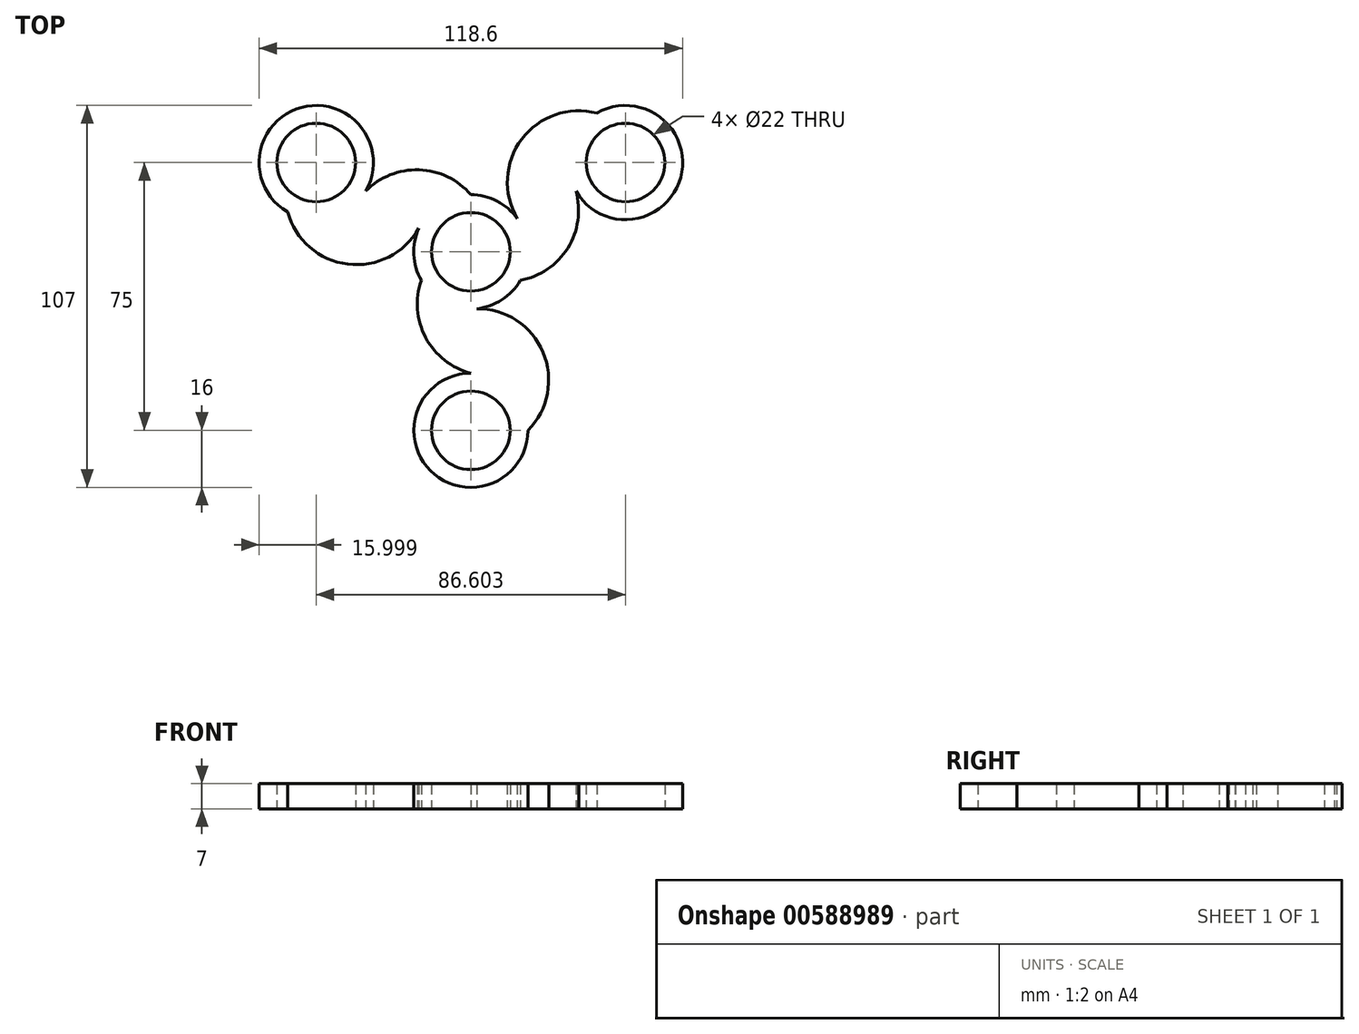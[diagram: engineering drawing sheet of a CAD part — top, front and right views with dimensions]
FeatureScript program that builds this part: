
annotation { "Feature Type Name" : "Feature", "Feature Type Description" : "" }
export const myFeature = defineFeature(function(context is Context, id is Id, definition is map)
    precondition{}
    {
        {
            var Q0;
            Q0=qCreatedBy(makeId("Top.planeOp"),FACE);
            var sketch = newSketch(context, id + "F0", { "sketchPlane" : qUnion([Q0])});
            skCircle(sketch, "E0", {"center": v(0, 0) * mm, "radius": 11 * mm});
            skCircle(sketch, "E1", {"center": v(0, 0) * mm, "radius": 16 * mm});
            skLineSegment(sketch, "E2", {"start": v(0, 0) * mm, "end": v(0, -50) * mm});
            skLineSegment(sketch, "E3", {"start": v(0, 0) * mm, "end": v(43.3, 25) * mm});
            skLineSegment(sketch, "E4", {"start": v(0, 0) * mm, "end": v(-43.3, 25) * mm});
            skCircle(sketch, "E5", {"center": v(-43.3, 25) * mm, "radius": 11 * mm});
            skCircle(sketch, "E6", {"center": v(43.3, 25) * mm, "radius": 11 * mm});
            skCircle(sketch, "E7", {"center": v(0, -50) * mm, "radius": 11 * mm});
            skCircle(sketch, "E8", {"center": v(0, -50) * mm, "radius": 16 * mm});
            skCircle(sketch, "E9", {"center": v(43.3, 25) * mm, "radius": 16 * mm});
            skCircle(sketch, "E10", {"center": v(-43.3, 25) * mm, "radius": 16 * mm});
            skLineSegment(sketch, "E11", {"start": v(0, 0) * mm, "end": v(0, 31.25) * mm});
            skLineSegment(sketch, "E12", {"start": v(0, 0) * mm, "end": v(44.93, 0) * mm});
            skLineSegment(sketch, "E13", {"start": v(0, 0) * mm, "end": v(39.74, -22.94) * mm});
            skLineSegment(sketch, "E14", {"start": v(0, 0) * mm, "end": v(-34.34, -19.83) * mm});
            skArc(sketch, "E15", {"start": v(13.86, -8) * mm, "mid": v(27.14, 1.08) * mm, "end": v(29.44, 17) * mm});
            skArc(sketch, "E16", {"start": v(0, 16) * mm, "mid": v(-14.5, 22.97) * mm, "end": v(-29.44, 17) * mm});
            skArc(sketch, "E17", {"start": v(-13.86, -8) * mm, "mid": v(-12.64, -24.04) * mm, "end": v(0, -34) * mm});
            skLineSegment(sketch, "E18", {"start": v(43.3, 25) * mm, "end": v(31.7, 45.08) * mm});
            skLineSegment(sketch, "E19", {"start": v(-43.3, 25) * mm, "end": v(-53.07, 8.08) * mm});
            skLineSegment(sketch, "E20", {"start": v(0, -50) * mm, "end": v(27.78, -50) * mm});
            skArc(sketch, "E21", {"start": v(35.3, 38.86) * mm, "mid": v(13.79, 30.93) * mm, "end": v(13.86, 8) * mm});
            skArc(sketch, "E22", {"start": v(16, -50) * mm, "mid": v(19.9, -27.4) * mm, "end": v(0, -16) * mm});
            skArc(sketch, "E23", {"start": v(-51.3, 11.14) * mm, "mid": v(-33.68, -3.53) * mm, "end": v(-13.86, 8) * mm});
            skSolve(sketch);
        }
        {
            var Q0;
            {var subQ0=sQuery(id+"F0.wireOp",EDGE,"E21");var subQ1=sQuery(id+"F0.wireOp",EDGE,"E1");var subQ3=makeQuery(id+"F0.imprint","INTERSECT",VERTEX,{"derivedFrom":[subQ1,subQ0]});Q0=makeQuery(id+"F0.imprint","IMPRINT",FACE,{"disambiguationData":[TD([[makeQuery(id+"F0.imprint","IMPRINT",EDGE,{"disambiguationData":[TD([[subQ3,1.0]])],"derivedFrom":subQ1}),1.0]])]});}
            var Q1;
            {var subQ0=sQuery(id+"F0.wireOp",EDGE,"E16");Q1=makeQuery(id+"F0.imprint","IMPRINT",FACE,{"disambiguationData":[TD([[makeQuery(id+"F0.imprint","IMPRINT",EDGE,{"derivedFrom":subQ0}),1.0]])]});}
            var Q2;
            {var subQ0=sQuery(id+"F0.wireOp",EDGE,"E17");Q2=makeQuery(id+"F0.imprint","IMPRINT",FACE,{"disambiguationData":[TD([[makeQuery(id+"F0.imprint","IMPRINT",EDGE,{"derivedFrom":subQ0}),1.0]])]});}
            var Q3;
            {var subQ0=sQuery(id+"F0.wireOp",EDGE,"E22");var subQ1=sQuery(id+"F0.wireOp",EDGE,"E1");var subQ3=makeQuery(id+"F0.imprint","INTERSECT",VERTEX,{"derivedFrom":[subQ1,subQ0]});Q3=makeQuery(id+"F0.imprint","IMPRINT",FACE,{"disambiguationData":[TD([[makeQuery(id+"F0.imprint","IMPRINT",EDGE,{"disambiguationData":[TD([[subQ3,1.0]])],"derivedFrom":subQ1}),1.0]])]});}
            var Q4;
            {var subQ0=sQuery(id+"F0.wireOp",EDGE,"E15");var subQ3=sQuery(id+"F0.wireOp",EDGE,"E12");var subQ5=makeQuery(id+"F0.imprint","INTERSECT",VERTEX,{"derivedFrom":[subQ3,subQ0]});Q4=makeQuery(id+"F0.imprint","IMPRINT",FACE,{"disambiguationData":[TD([[makeQuery(id+"F0.imprint","IMPRINT",EDGE,{"disambiguationData":[TD([[subQ5,1.0]])],"derivedFrom":subQ3}),-1.0]])]});}
            var Q5;
            {var subQ1=sQuery(id+"F0.wireOp",EDGE,"E2");var subQ3=sQuery(id+"F0.wireOp",EDGE,"E7");var subQ4=makeQuery(id+"F0.imprint","INTERSECT",VERTEX,{"derivedFrom":[subQ1,subQ3]});Q5=makeQuery(id+"F0.imprint","IMPRINT",FACE,{"disambiguationData":[TD([[makeQuery(id+"F0.imprint","IMPRINT",EDGE,{"disambiguationData":[TD([[subQ4,-1.0]])],"derivedFrom":subQ3}),-1.0]])]});}
            var Q6;
            {var subQ1=sQuery(id+"F0.wireOp",EDGE,"E3");var subQ3=sQuery(id+"F0.wireOp",EDGE,"E6");var subQ4=makeQuery(id+"F0.imprint","INTERSECT",VERTEX,{"derivedFrom":[subQ1,subQ3]});Q6=makeQuery(id+"F0.imprint","IMPRINT",FACE,{"disambiguationData":[TD([[makeQuery(id+"F0.imprint","IMPRINT",EDGE,{"disambiguationData":[TD([[subQ4,-1.0]])],"derivedFrom":subQ3}),-1.0]])]});}
            var Q7;
            {var subQ1=sQuery(id+"F0.wireOp",EDGE,"E4");var subQ3=sQuery(id+"F0.wireOp",EDGE,"E5");var subQ4=makeQuery(id+"F0.imprint","INTERSECT",VERTEX,{"derivedFrom":[subQ1,subQ3]});Q7=makeQuery(id+"F0.imprint","IMPRINT",FACE,{"disambiguationData":[TD([[makeQuery(id+"F0.imprint","IMPRINT",EDGE,{"disambiguationData":[TD([[subQ4,-1.0]])],"derivedFrom":subQ3}),-1.0]])]});}
            var Q8;
            {var subQ0=sQuery(id+"F0.wireOp",EDGE,"xA9ERZAI-CVpG-Lb7w-0VQH-98zOtqBdUd82");var subQ1=sQuery(id+"F0.wireOp",EDGE,"E0");var subQ2=makeQuery(id+"F0.imprint","INTERSECT",VERTEX,{"derivedFrom":[subQ1,subQ0]});Q8=makeQuery(id+"F0.imprint","IMPRINT",FACE,{"disambiguationData":[TD([[makeQuery(id+"F0.imprint","IMPRINT",EDGE,{"disambiguationData":[TD([[subQ2,-1.0]])],"derivedFrom":subQ1}),-1.0]])]});}
            var Q9;
            {var subQ3=sQuery(id+"F0.wireOp",EDGE,"E12");var subQ5=sQuery(id+"F0.wireOp",EDGE,"E15");var subQ7=makeQuery(id+"F0.imprint","INTERSECT",VERTEX,{"derivedFrom":[subQ3,subQ5]});Q9=makeQuery(id+"F0.imprint","IMPRINT",FACE,{"disambiguationData":[TD([[makeQuery(id+"F0.imprint","IMPRINT",EDGE,{"disambiguationData":[TD([[subQ7,1.0]])],"derivedFrom":subQ3}),1.0]])]});}
            var Q10;
            {var subQ0=sQuery(id+"F0.wireOp",EDGE,"E21");var subQ2=sQuery(id+"F0.wireOp",EDGE,"E1");var subQ4=makeQuery(id+"F0.imprint","INTERSECT",VERTEX,{"derivedFrom":[subQ2,subQ0]});Q10=makeQuery(id+"F0.imprint","IMPRINT",FACE,{"disambiguationData":[TD([[makeQuery(id+"F0.imprint","IMPRINT",EDGE,{"disambiguationData":[TD([[subQ4,1.0]])],"derivedFrom":subQ2}),-1.0]])]});}
            var Q11;
            {var subQ0=sQuery(id+"F0.wireOp",EDGE,"E22");var subQ2=sQuery(id+"F0.wireOp",EDGE,"E1");var subQ4=makeQuery(id+"F0.imprint","INTERSECT",VERTEX,{"derivedFrom":[subQ2,subQ0]});Q11=makeQuery(id+"F0.imprint","IMPRINT",FACE,{"disambiguationData":[TD([[makeQuery(id+"F0.imprint","IMPRINT",EDGE,{"disambiguationData":[TD([[subQ4,1.0]])],"derivedFrom":subQ2}),-1.0]])]});}
            var Q12;
            {var subQ1=sQuery(id+"F0.wireOp",EDGE,"E2");var subQ3=sQuery(id+"F0.wireOp",EDGE,"E7");var subQ4=makeQuery(id+"F0.imprint","INTERSECT",VERTEX,{"derivedFrom":[subQ1,subQ3]});Q12=makeQuery(id+"F0.imprint","IMPRINT",FACE,{"disambiguationData":[TD([[makeQuery(id+"F0.imprint","IMPRINT",EDGE,{"disambiguationData":[TD([[subQ4,1.0]])],"derivedFrom":subQ3}),-1.0]])]});}
            var Q13;
            {var subQ1=sQuery(id+"F0.wireOp",EDGE,"E3");var subQ3=sQuery(id+"F0.wireOp",EDGE,"E6");var subQ4=makeQuery(id+"F0.imprint","INTERSECT",VERTEX,{"derivedFrom":[subQ1,subQ3]});Q13=makeQuery(id+"F0.imprint","IMPRINT",FACE,{"disambiguationData":[TD([[makeQuery(id+"F0.imprint","IMPRINT",EDGE,{"disambiguationData":[TD([[subQ4,1.0]])],"derivedFrom":subQ3}),-1.0]])]});}
            var Q14;
            {var subQ1=sQuery(id+"F0.wireOp",EDGE,"E4");var subQ3=sQuery(id+"F0.wireOp",EDGE,"E5");var subQ4=makeQuery(id+"F0.imprint","INTERSECT",VERTEX,{"derivedFrom":[subQ1,subQ3]});Q14=makeQuery(id+"F0.imprint","IMPRINT",FACE,{"disambiguationData":[TD([[makeQuery(id+"F0.imprint","IMPRINT",EDGE,{"disambiguationData":[TD([[subQ4,1.0]])],"derivedFrom":subQ3}),-1.0]])]});}
            var Q15;
            {var subQ3=sQuery(id+"F0.wireOp",EDGE,"E0");var subQ6=sQuery(id+"F0.wireOp",EDGE,"E3");var subQ8=makeQuery(id+"F0.imprint","INTERSECT",VERTEX,{"derivedFrom":[subQ3,subQ6]});Q15=makeQuery(id+"F0.imprint","IMPRINT",FACE,{"disambiguationData":[TD([[makeQuery(id+"F0.imprint","IMPRINT",EDGE,{"disambiguationData":[TD([[subQ8,-1.0]])],"derivedFrom":subQ3}),-1.0]])]});}
            var Q16;
            {var subQ0=sQuery(id+"F0.wireOp",EDGE,"E11");var subQ1=sQuery(id+"F0.wireOp",EDGE,"E0");var subQ2=makeQuery(id+"F0.imprint","INTERSECT",VERTEX,{"derivedFrom":[subQ1,subQ0]});Q16=makeQuery(id+"F0.imprint","IMPRINT",FACE,{"disambiguationData":[TD([[makeQuery(id+"F0.imprint","IMPRINT",EDGE,{"disambiguationData":[TD([[subQ2,-1.0]])],"derivedFrom":subQ1}),-1.0]])]});}
            var Q17;
            {var subQ0=sQuery(id+"F0.wireOp",EDGE,"E14");var subQ1=sQuery(id+"F0.wireOp",EDGE,"E0");var subQ2=makeQuery(id+"F0.imprint","INTERSECT",VERTEX,{"derivedFrom":[subQ1,subQ0]});Q17=makeQuery(id+"F0.imprint","IMPRINT",FACE,{"disambiguationData":[TD([[makeQuery(id+"F0.imprint","IMPRINT",EDGE,{"disambiguationData":[TD([[subQ2,-1.0]])],"derivedFrom":subQ1}),-1.0]])]});}
            var Q18;
            {var subQ3=sQuery(id+"F0.wireOp",EDGE,"E0");var subQ6=sQuery(id+"F0.wireOp",EDGE,"E2");var subQ8=makeQuery(id+"F0.imprint","INTERSECT",VERTEX,{"derivedFrom":[subQ3,subQ6]});Q18=makeQuery(id+"F0.imprint","IMPRINT",FACE,{"disambiguationData":[TD([[makeQuery(id+"F0.imprint","IMPRINT",EDGE,{"disambiguationData":[TD([[subQ8,-1.0]])],"derivedFrom":subQ3}),-1.0]])]});}
            var Q19;
            {var subQ0=sQuery(id+"F0.wireOp",EDGE,"E12");var subQ1=sQuery(id+"F0.wireOp",EDGE,"E0");var subQ2=makeQuery(id+"F0.imprint","INTERSECT",VERTEX,{"derivedFrom":[subQ1,subQ0]});Q19=makeQuery(id+"F0.imprint","IMPRINT",FACE,{"disambiguationData":[TD([[makeQuery(id+"F0.imprint","IMPRINT",EDGE,{"disambiguationData":[TD([[subQ2,1.0]])],"derivedFrom":subQ1}),-1.0]])]});}
            var Q20;
            {var subQ3=sQuery(id+"F0.wireOp",EDGE,"E23");var subQ7=makeQuery(id+"F0.imprint","INTERSECT",VERTEX,{"derivedFrom":[sQuery(id+"F0.wireOp",EDGE,"xA9ERZAI-CVpG-Lb7w-0VQH-98zOtqBdUd82"),subQ3]});Q20=makeQuery(id+"F0.imprint","IMPRINT",FACE,{"disambiguationData":[TD([[makeQuery(id+"F0.imprint","IMPRINT",EDGE,{"disambiguationData":[TD([[subQ7,-1.0]])],"derivedFrom":subQ3}),1.0]])]});}
            var Q21;
            {var subQ3=sQuery(id+"F0.wireOp",EDGE,"E0");var subQ6=sQuery(id+"F0.wireOp",EDGE,"E4");var subQ8=makeQuery(id+"F0.imprint","INTERSECT",VERTEX,{"derivedFrom":[subQ3,subQ6]});Q21=makeQuery(id+"F0.imprint","IMPRINT",FACE,{"disambiguationData":[TD([[makeQuery(id+"F0.imprint","IMPRINT",EDGE,{"disambiguationData":[TD([[subQ8,-1.0]])],"derivedFrom":subQ3}),-1.0]])]});}
            var Q22;
            {var subQ0=sQuery(id+"F0.wireOp",EDGE,"E3");var subQ1=sQuery(id+"F0.wireOp",EDGE,"E0");var subQ2=makeQuery(id+"F0.imprint","INTERSECT",VERTEX,{"derivedFrom":[subQ1,subQ0]});Q22=makeQuery(id+"F0.imprint","IMPRINT",FACE,{"disambiguationData":[TD([[makeQuery(id+"F0.imprint","IMPRINT",EDGE,{"disambiguationData":[TD([[subQ2,1.0]])],"derivedFrom":subQ1}),-1.0]])]});}
            var Q23;
            {var subQ0=sQuery(id+"F0.wireOp",EDGE,"xA9ERZAI-CVpG-Lb7w-0VQH-98zOtqBdUd82");var subQ1=sQuery(id+"F0.wireOp",EDGE,"E1");var subQ2=makeQuery(id+"F0.imprint","INTERSECT",VERTEX,{"derivedFrom":[subQ1,subQ0]});Q23=makeQuery(id+"F0.imprint","IMPRINT",FACE,{"disambiguationData":[TD([[makeQuery(id+"F0.imprint","IMPRINT",EDGE,{"disambiguationData":[TD([[subQ2,1.0]])],"derivedFrom":subQ1}),-1.0]])]});}
            var Q24;
            {var subQ0=sQuery(id+"F0.wireOp",EDGE,"E23");var subQ2=sQuery(id+"F0.wireOp",EDGE,"E1");var subQ4=makeQuery(id+"F0.imprint","INTERSECT",VERTEX,{"derivedFrom":[subQ2,subQ0]});Q24=makeQuery(id+"F0.imprint","IMPRINT",FACE,{"disambiguationData":[TD([[makeQuery(id+"F0.imprint","IMPRINT",EDGE,{"disambiguationData":[TD([[subQ4,1.0]])],"derivedFrom":subQ2}),-1.0]])]});}
            extrude(context, id + "F1", {"entities" : qUnion([Q0, Q1, Q2, Q3, Q4, Q5, Q6, Q7, Q8, Q9, Q10, Q11, Q12, Q13, Q14, Q15, Q16, Q17, Q18, Q19, Q20, Q21, Q22, Q23, Q24]), "depth" : 7 * mm, "offsetDistance" : 25 * mm});
        }
    });
